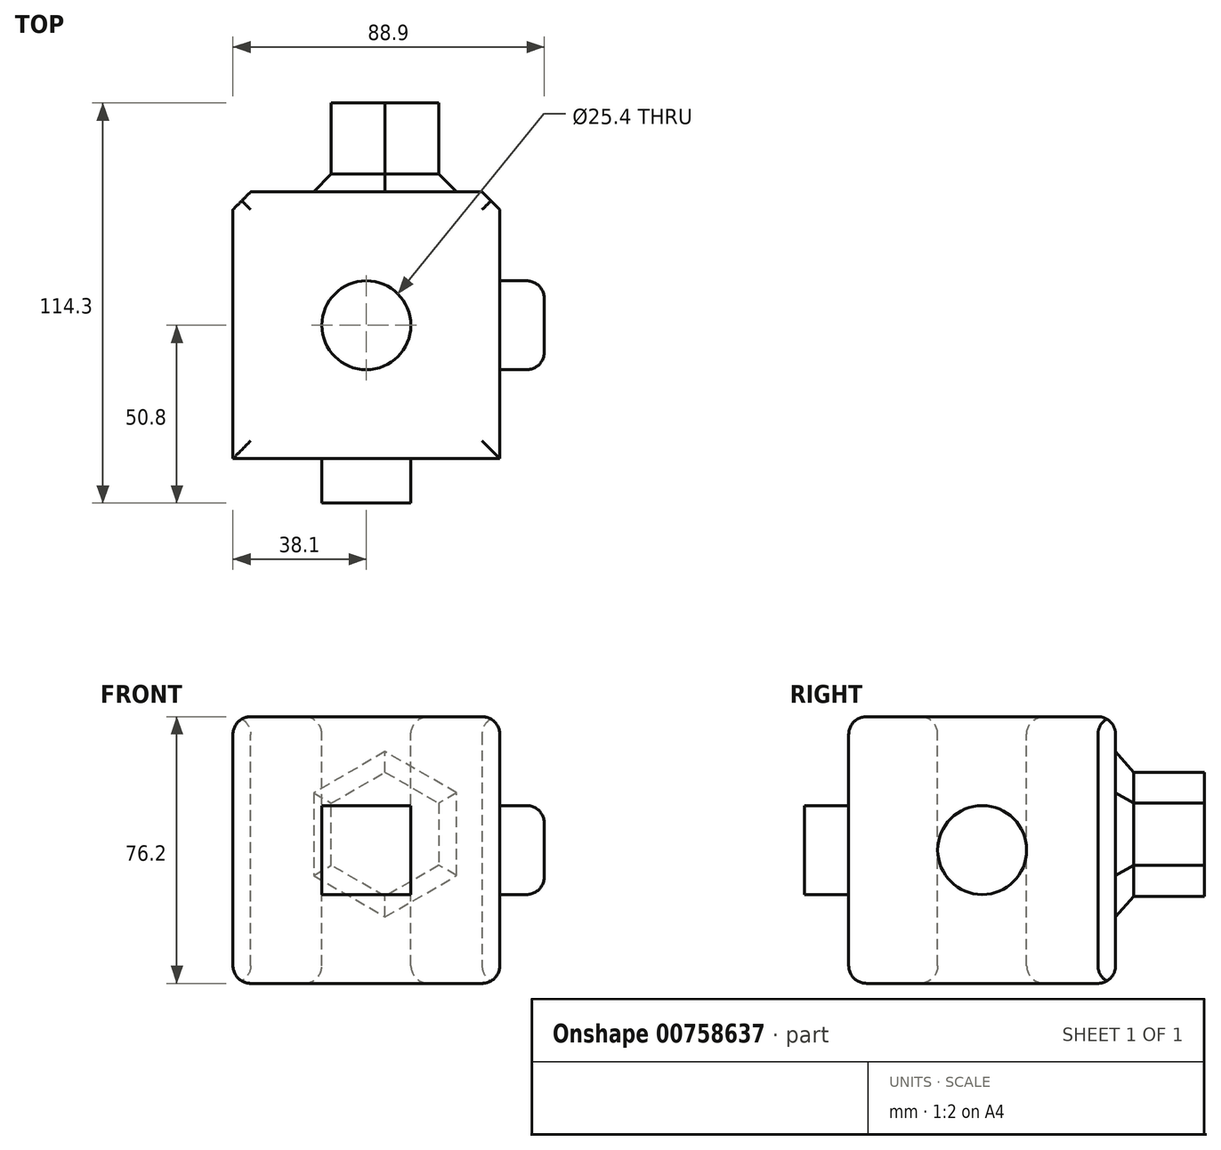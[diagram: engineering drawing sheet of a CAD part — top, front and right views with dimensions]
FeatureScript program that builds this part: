
annotation { "Feature Type Name" : "Feature", "Feature Type Description" : "" }
export const myFeature = defineFeature(function(context is Context, id is Id, definition is map)
    precondition{}
    {
        {
            var Q0;
            Q0=qCreatedBy(makeId("Front.planeOp"),FACE);
            var sketch = newSketch(context, id + "F0", { "sketchPlane" : qUnion([Q0])});
            skLineSegment(sketch, "E0.bottom", {"start": v(-76.2, -2.37) * mm, "end": v(0, -2.37) * mm});
            skLineSegment(sketch, "E0.top", {"start": v(-76.2, -78.57) * mm, "end": v(0, -78.57) * mm});
            skLineSegment(sketch, "E0.left", {"start": v(-76.2, -2.37) * mm, "end": v(-76.2, -78.57) * mm});
            skLineSegment(sketch, "E0.right", {"start": v(0, -2.37) * mm, "end": v(0, -78.57) * mm});
            skSolve(sketch);
        }
        {
            var Q0;
            Q0=makeQuery(id+"F0.imprint","IMPRINT",FACE,{"disambiguationData":[TD([[makeQuery(id+"F0.imprint","IMPRINT",EDGE,{"derivedFrom":sQuery(id+"F0.wireOp",EDGE,"E0.bottom")}),-1.0]])]});
            extrude(context, id + "F1", {"entities" : qUnion([Q0]), "oppositeDirection" : true, "depth" : 76.2 * mm, "offsetDistance" : 25.4 * mm});
        }
        {
            var Q0;
            Q0=makeQuery(id+"F1.opExtrude","CAP_FACE",FACE,{"disambiguationData":[OSD([sQuery(id+"F0.wireOp",EDGE,"E0.bottom"),sQuery(id+"F0.wireOp",EDGE,"E0.top"),sQuery(id+"F0.wireOp",EDGE,"E0.left"),sQuery(id+"F0.wireOp",EDGE,"E0.right")])],"isStart":true});
            var sketch = newSketch(context, id + "F2", { "sketchPlane" : qUnion([Q0])});
            skLineSegment(sketch, "E1.bottom", {"start": v(-50.8, -27.77) * mm, "end": v(-25.4, -27.77) * mm});
            skLineSegment(sketch, "E1.top", {"start": v(-50.8, -53.17) * mm, "end": v(-25.4, -53.17) * mm});
            skLineSegment(sketch, "E1.left", {"start": v(-50.8, -27.77) * mm, "end": v(-50.8, -53.17) * mm});
            skLineSegment(sketch, "E1.right", {"start": v(-25.4, -27.77) * mm, "end": v(-25.4, -53.17) * mm});
            skSolve(sketch);
        }
        {
            var Q0;
            Q0=makeQuery(id+"F2.imprint","IMPRINT",FACE,{"disambiguationData":[TD([[makeQuery(id+"F2.imprint","IMPRINT",EDGE,{"derivedFrom":sQuery(id+"F2.wireOp",EDGE,"E1.bottom")}),-1.0]])]});
            extrude(context, id + "F3", {"entities" : qUnion([Q0]), "operationType" : NewBodyOperationType.ADD, "depth" : 12.7 * mm, "offsetDistance" : 25.4 * mm});
        }
        {
            var Q0;
            Q0=makeQuery(id+"F1.opExtrude","SWEPT_FACE",FACE,{"disambiguationData":[OSD([sQuery(id+"F0.wireOp",EDGE,"E0.right")])]});
            var sketch = newSketch(context, id + "F4", { "sketchPlane" : qUnion([Q0])});
            skCircle(sketch, "E2", {"center": v(38.1, -40.47) * mm, "radius": 12.7 * mm});
            skSolve(sketch);
        }
        {
            var Q0;
            Q0=makeQuery(id+"F4.imprint","IMPRINT",FACE,{"disambiguationData":[TD([[makeQuery(id+"F4.imprint","IMPRINT",EDGE,{"derivedFrom":sQuery(id+"F4.wireOp",EDGE,"E2")}),1.0]])]});
            extrude(context, id + "F5", {"entities" : qUnion([Q0]), "operationType" : NewBodyOperationType.ADD, "depth" : 12.7 * mm, "offsetDistance" : 25.4 * mm});
        }
        {
            var Q0;
            Q0=makeQuery(id+"F1.opExtrude","SWEPT_FACE",FACE,{"disambiguationData":[OSD([sQuery(id+"F0.wireOp",EDGE,"E0.bottom")])]});
            var sketch = newSketch(context, id + "F6", { "sketchPlane" : qUnion([Q0])});
            skPoint(sketch, "E3", {"position": v(-38.1, 38.1) * mm});
            skSolve(sketch);
        }
        {
            var Q0;
            Q0=sQuery(id+"F6.wireOp",VERTEX,"E3");
            var Q1;
            Q1=makeQuery(id+"F1.opExtrude","SWEPT_BODY",BODY,{"disambiguationData":[OSD([sQuery(id+"F0.wireOp",EDGE,"E0.bottom"),sQuery(id+"F0.wireOp",EDGE,"E0.top"),sQuery(id+"F0.wireOp",EDGE,"E0.left"),sQuery(id+"F0.wireOp",EDGE,"E0.right")])]});
            hole(context, id + "F7", {"style" : HoleStyle.SIMPLE, "endStyle" : HoleEndStyle.THROUGH, "holeDiameter" : 25.4 * mm, "majorDiameter" : 6.35 * mm, "isTappedThrough" : true, "tappedDepth" : 12.7 * mm, "tapClearance" : 3, "locations" : qUnion([Q0]), "scope" : qUnion([Q1])});
        }
        {
            var Q0;
            Q0=makeQuery(id+"F1.opExtrude","CAP_FACE",FACE,{"disambiguationData":[OSD([sQuery(id+"F0.wireOp",EDGE,"E0.bottom"),sQuery(id+"F0.wireOp",EDGE,"E0.top"),sQuery(id+"F0.wireOp",EDGE,"E0.left"),sQuery(id+"F0.wireOp",EDGE,"E0.right")])],"isStart":false});
            var sketch = newSketch(context, id + "F8", { "sketchPlane" : qUnion([Q0])});
            skCircle(sketch, "E4.cCircle", {"center": v(32.75, -35.97) * mm, "radius": 15.36 * mm, "construction": true});
            skLineSegment(sketch, "E4.0", {"start": v(17.39, -44.84) * mm, "end": v(17.39, -27.1) * mm});
            skLineSegment(sketch, "E4.1", {"start": v(17.39, -27.1) * mm, "end": v(32.75, -18.24) * mm});
            skLineSegment(sketch, "E4.2", {"start": v(32.75, -18.24) * mm, "end": v(48.1, -27.1) * mm});
            skLineSegment(sketch, "E4.3", {"start": v(48.1, -27.1) * mm, "end": v(48.1, -44.84) * mm});
            skLineSegment(sketch, "E4.4", {"start": v(48.1, -44.84) * mm, "end": v(32.75, -53.7) * mm});
            skLineSegment(sketch, "E4.5", {"start": v(32.75, -53.7) * mm, "end": v(17.39, -44.84) * mm});
            skPoint(sketch, "E4.0.midPoint", {"position": v(17.39, -35.97) * mm});
            skSolve(sketch);
        }
        {
            var Q0;
            Q0=makeQuery(id+"F8.imprint","IMPRINT",FACE,{"disambiguationData":[TD([[makeQuery(id+"F8.imprint","IMPRINT",EDGE,{"derivedFrom":sQuery(id+"F8.wireOp",EDGE,"E4.0")}),-1.0]])]});
            extrude(context, id + "F9", {"entities" : qUnion([Q0]), "operationType" : NewBodyOperationType.ADD, "depth" : 25.4 * mm, "offsetDistance" : 25.4 * mm});
        }
        {
            var Q0;
            Q0=makeQuery(id+"F1.opExtrude","SWEPT_FACE",FACE,{"disambiguationData":[OSD([sQuery(id+"F0.wireOp",EDGE,"E0.bottom")])]});
            fillet(context, id + "F10", {"entities" : qUnion([Q0]), "radius" : 5.08 * mm, "tangentPropagation" : true, "allowEdgeOverflow" : false});
        }
        {
            var Q0;
            Q0=makeQuery(id+"F5.opExtrude","CAP_FACE",FACE,{"disambiguationData":[OSD([sQuery(id+"F4.wireOp",EDGE,"E2")])],"isStart":false});
            fillet(context, id + "F11", {"entities" : qUnion([Q0]), "radius" : 5.08 * mm, "tangentPropagation" : true, "allowEdgeOverflow" : false});
        }
        {
            var Q0;
            Q0=makeQuery(id+"F1.opExtrude","SWEPT_FACE",FACE,{"disambiguationData":[OSD([sQuery(id+"F0.wireOp",EDGE,"E0.top")])]});
            fillet(context, id + "F12", {"entities" : qUnion([Q0]), "radius" : 5.08 * mm, "tangentPropagation" : true, "allowEdgeOverflow" : false});
        }
        {
            var Q0;
            Q0=makeQuery(id+"F1.opExtrude","CAP_FACE",FACE,{"disambiguationData":[OSD([sQuery(id+"F0.wireOp",EDGE,"E0.bottom"),sQuery(id+"F0.wireOp",EDGE,"E0.top"),sQuery(id+"F0.wireOp",EDGE,"E0.left"),sQuery(id+"F0.wireOp",EDGE,"E0.right")])],"isStart":false});
            chamfer(context, id + "F13", {"entities" : qUnion([Q0]), "width" : 5.08 * mm, "tangentPropagation" : true});
        }
    });
